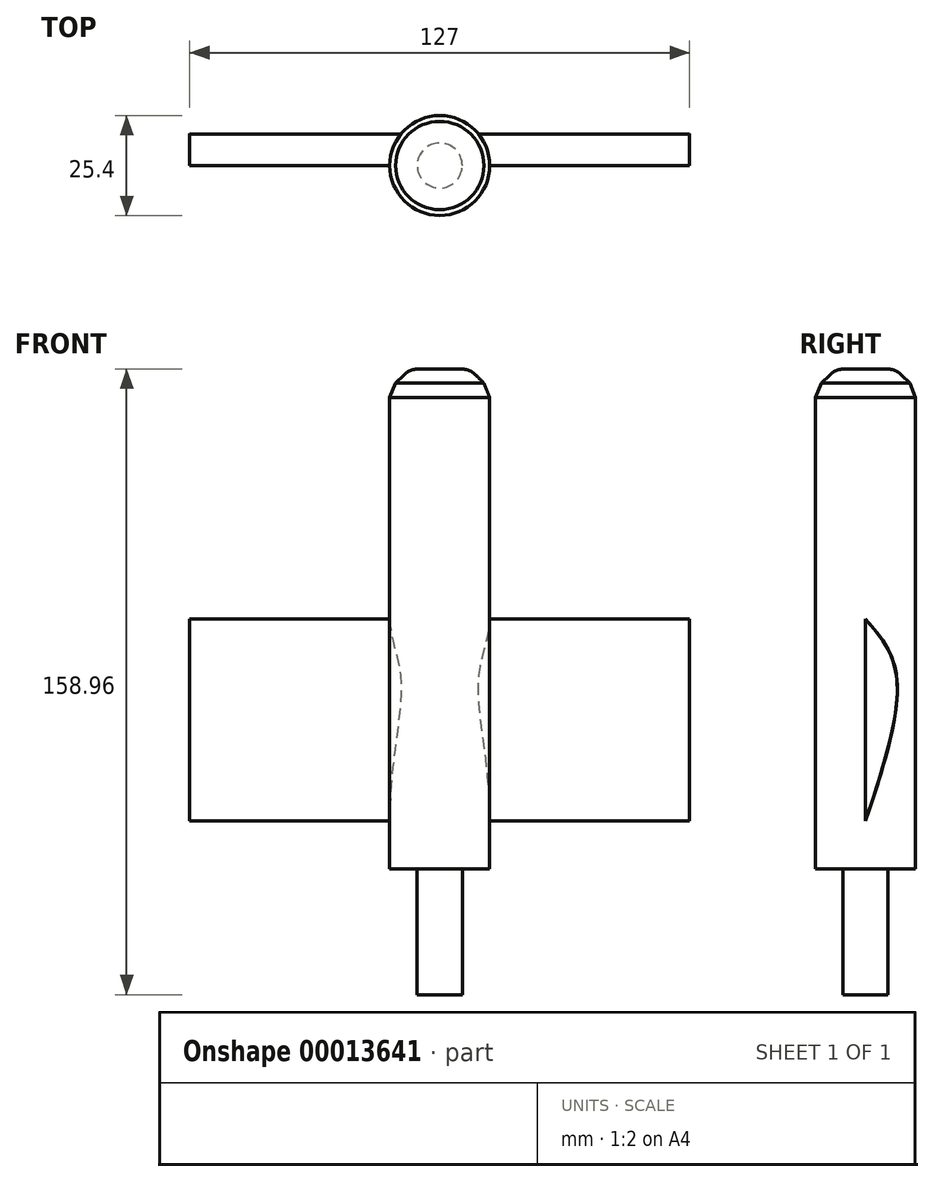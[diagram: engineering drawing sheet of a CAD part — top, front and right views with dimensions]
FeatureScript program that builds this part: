
annotation { "Feature Type Name" : "Feature", "Feature Type Description" : "" }
export const myFeature = defineFeature(function(context is Context, id is Id, definition is map)
    precondition{}
    {
        {
            var Q0;
            Q0=qCreatedBy(makeId("Top.planeOp"),FACE);
            var sketch = newSketch(context, id + "F0", { "sketchPlane" : qUnion([Q0])});
            skCircle(sketch, "E0", {"center": v(0, 0) * mm, "radius": 12.7 * mm});
            skSolve(sketch);
        }
        {
            var Q0;
            Q0=makeQuery(id+"F0.imprint","IMPRINT",FACE,{"disambiguationData":[TD([[makeQuery(id+"F0.imprint","IMPRINT",EDGE,{"derivedFrom":sQuery(id+"F0.wireOp",EDGE,"E0")}),1.0]])]});
            extrude(context, id + "F1", {"entities" : qUnion([Q0]), "endBound" : BoundingType.SYMMETRIC, "oppositeDirection" : true, "depth" : 127 * mm});
        }
        {
            var Q0;
            Q0=qCreatedBy(makeId("Right.planeOp"),FACE);
            var sketch = newSketch(context, id + "F2", { "sketchPlane" : qUnion([Q0])});
            skFitSpline(sketch, "E1", {"points": [v(0, 0) * mm, v(7.8, -14.11) * mm, v(0, -51.36) * mm], "startDerivative": vector(26.2, -30.73) * mm, "endDerivative": vector(-22.75, -69.27) * mm});
            skLineSegment(sketch, "E2", {"start": v(0, -51.36) * mm, "end": v(0, 0) * mm});
            skSolve(sketch);
        }
        {
            var Q0;
            Q0 = qSketchRegion(id + "F2", true);
            extrude(context, id + "F3", {"entities" : qUnion([Q0]), "operationType" : NewBodyOperationType.ADD, "endBound" : BoundingType.SYMMETRIC, "depth" : 127 * mm});
        }
        {
            var Q0;
            Q0=makeQuery(id+"F1.opExtrude","CAP_FACE",FACE,{"disambiguationData":[OSD([sQuery(id+"F0.wireOp",EDGE,"E0")])],"isStart":true});
            chamfer(context, id + "F4", {"entities" : qUnion([Q0]), "width" : 5.08 * mm, "tangentPropagation" : true});
        }
        {
            var Q0;
            {var subQ0=sQuery(id+"F0.wireOp",EDGE,"E0");Q0=makeQuery(id+"F4.opChamfer","BLEND_EDGE",EDGE,{"blendedFrom":[makeQuery(id+"F1.opExtrude","CAP_EDGE",EDGE,{"disambiguationData":[OSD([subQ0])],"isStart":true}),makeQuery(id+"F1.opExtrude","SWEPT_FACE",FACE,{"disambiguationData":[OSD([subQ0])]})],"blendedInto":[makeQuery(id+"F1.opExtrude","SWEPT_FACE",FACE,{"disambiguationData":[OSD([subQ0])]})]});}
            chamfer(context, id + "F5", {"entities" : qUnion([Q0]), "width" : 5.08 * mm, "tangentPropagation" : true});
        }
        {
            var Q0;
            Q0=makeQuery(id+"F1.opExtrude","CAP_FACE",FACE,{"disambiguationData":[OSD([sQuery(id+"F0.wireOp",EDGE,"E0")])],"isStart":true});
            fillet(context, id + "F6", {"entities" : qUnion([Q0]), "radius" : 5.08 * mm, "tangentPropagation" : true, "allowEdgeOverflow" : false});
        }
        {
            var Q0;
            Q0=makeQuery(id+"F1.opExtrude","CAP_FACE",FACE,{"disambiguationData":[OSD([sQuery(id+"F0.wireOp",EDGE,"E0")])],"isStart":false});
            var sketch = newSketch(context, id + "F7", { "sketchPlane" : qUnion([Q0])});
            skCircle(sketch, "E3", {"center": v(0, 0) * mm, "radius": 5.72 * mm});
            skSolve(sketch);
        }
        {
            var Q0;
            Q0=makeQuery(id+"F7.imprint","IMPRINT",FACE,{"disambiguationData":[TD([[makeQuery(id+"F7.imprint","IMPRINT",EDGE,{"derivedFrom":sQuery(id+"F7.wireOp",EDGE,"E3")}),1.0]])]});
            extrude(context, id + "F8", {"entities" : qUnion([Q0]), "operationType" : NewBodyOperationType.ADD, "depth" : 31.96 * mm});
        }
    });
